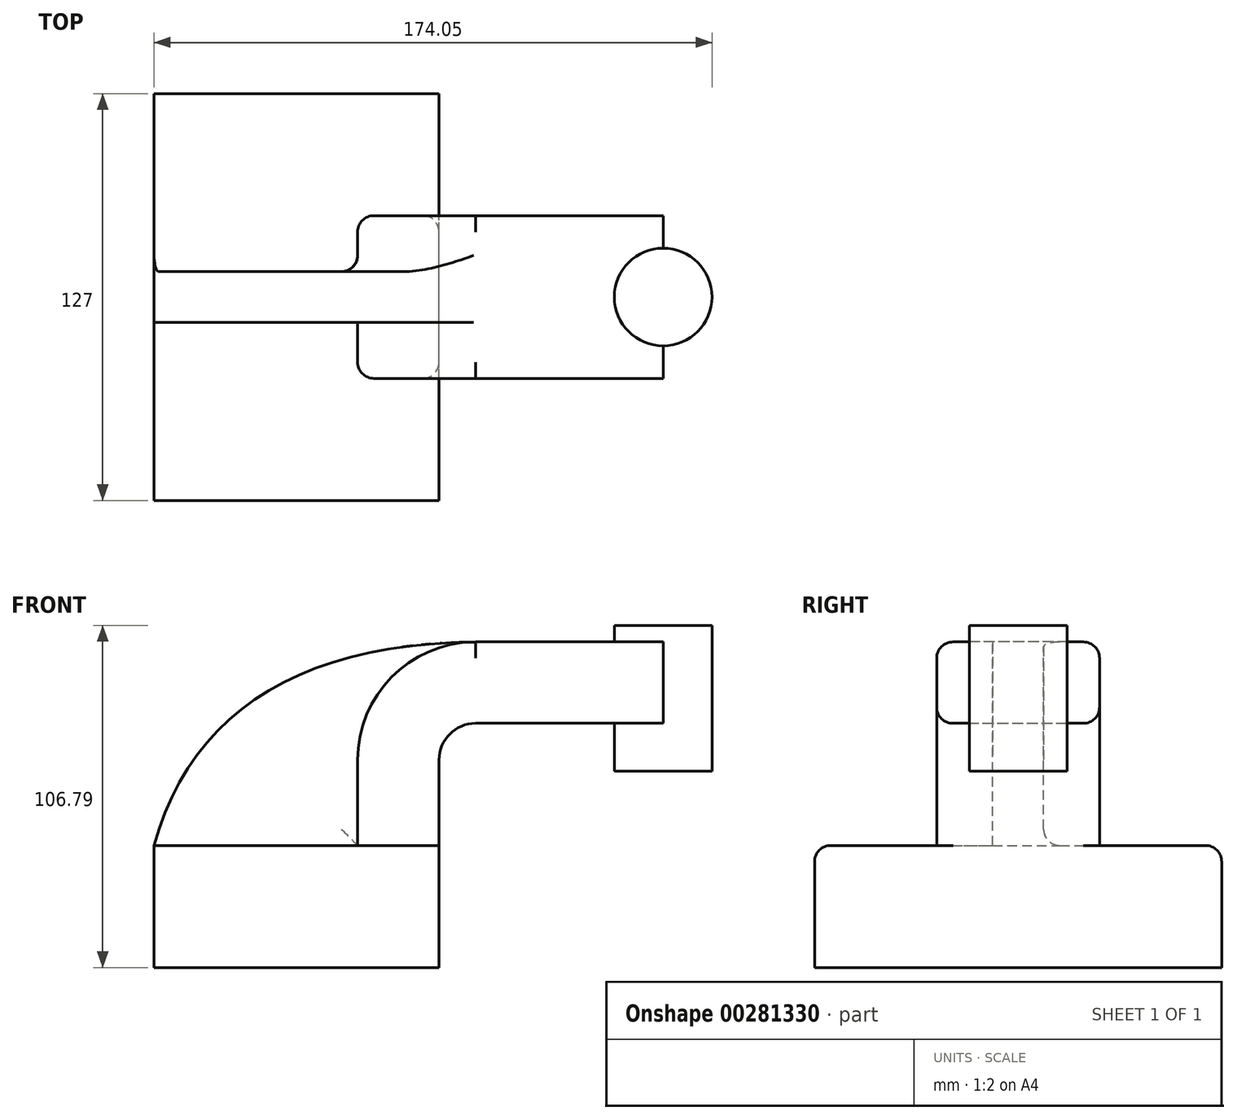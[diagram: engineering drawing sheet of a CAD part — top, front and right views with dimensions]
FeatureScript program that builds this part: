
annotation { "Feature Type Name" : "Feature", "Feature Type Description" : "" }
export const myFeature = defineFeature(function(context is Context, id is Id, definition is map)
    precondition{}
    {
        {
            var Q0;
            Q0=qCreatedBy(makeId("Front.planeOp"),FACE);
            var sketch = newSketch(context, id + "F0", { "sketchPlane" : qUnion([Q0])});
            skLineSegment(sketch, "E0.bottom", {"start": v(44.45, -19.05) * mm, "end": v(-44.45, -19.05) * mm});
            skLineSegment(sketch, "E0.top", {"start": v(44.45, 19.05) * mm, "end": v(-44.45, 19.05) * mm});
            skLineSegment(sketch, "E0.left", {"start": v(44.45, -19.05) * mm, "end": v(44.45, 19.05) * mm});
            skLineSegment(sketch, "E0.right", {"start": v(-44.45, -19.05) * mm, "end": v(-44.45, 19.05) * mm});
            skPoint(sketch, "E0.middle", {"position": v(0, 0) * mm});
            skLineSegment(sketch, "E1.bottom", {"start": v(129.6, 42.19) * mm, "end": v(99.12, 42.19) * mm});
            skLineSegment(sketch, "E1.top", {"start": v(129.6, 87.74) * mm, "end": v(99.12, 87.74) * mm});
            skLineSegment(sketch, "E1.left", {"start": v(129.6, 42.19) * mm, "end": v(129.6, 87.74) * mm});
            skLineSegment(sketch, "E1.right", {"start": v(99.12, 42.19) * mm, "end": v(99.12, 87.74) * mm});
            skPoint(sketch, "E1.middle", {"position": v(114.36, 64.96) * mm});
            skLineSegment(sketch, "E2", {"start": v(44.45, 19.05) * mm, "end": v(44.45, 45.77) * mm});
            skArc(sketch, "E3", {"start": v(44.45, 45.77) * mm, "mid": v(47.79, 53.83) * mm, "end": v(55.85, 57.16) * mm});
            skArc(sketch, "E4.1", {"start": v(19.05, 45.77) * mm, "mid": v(29.83, 71.79) * mm, "end": v(55.85, 82.56) * mm});
            skLineSegment(sketch, "E4.2", {"start": v(19.05, 19.05) * mm, "end": v(19.05, 45.77) * mm});
            skLineSegment(sketch, "E5", {"start": v(55.85, 82.56) * mm, "end": v(114.36, 82.56) * mm});
            skLineSegment(sketch, "E6", {"start": v(114.36, 57.16) * mm, "end": v(55.85, 57.16) * mm});
            skFitSpline(sketch, "E7", {"points": [v(-44.45, 19.05) * mm, v(55.85, 82.56) * mm], "startDerivative": vector(33.5, 123.73) * mm, "endDerivative": vector(164.87, 1.22) * mm});
            skLineSegment(sketch, "E8", {"start": v(114.36, 87.74) * mm, "end": v(114.36, 42.19) * mm});
            skSolve(sketch);
        }
        {
            var Q0;
            Q0=makeQuery(id+"F0.imprint","IMPRINT",FACE,{"disambiguationData":[TD([[makeQuery(id+"F0.imprint","IMPRINT",EDGE,{"derivedFrom":sQuery(id+"F0.wireOp",EDGE,"E0.bottom")}),-1.0]])]});
            extrude(context, id + "F1", {"entities" : qUnion([Q0]), "endBound" : BoundingType.SYMMETRIC, "depth" : 127 * mm});
        }
        {
            var Q0;
            {var subQ1=sQuery(id+"F0.wireOp",EDGE,"E2");Q0=makeQuery(id+"F0.imprint","IMPRINT",FACE,{"disambiguationData":[TD([[makeQuery(id+"F0.imprint","IMPRINT",EDGE,{"derivedFrom":subQ1}),1.0]])]});}
            var Q1;
            {var subQ0=sQuery(id+"F0.wireOp",EDGE,"E6");var subQ1=sQuery(id+"F0.wireOp",EDGE,"E1.right");var subQ2=makeQuery(id+"F0.imprint","INTERSECT",VERTEX,{"derivedFrom":[subQ1,subQ0]});Q1=makeQuery(id+"F0.imprint","IMPRINT",FACE,{"disambiguationData":[TD([[makeQuery(id+"F0.imprint","IMPRINT",EDGE,{"disambiguationData":[TD([[subQ2,-1.0]])],"derivedFrom":subQ1}),-1.0]])]});}
            extrude(context, id + "F2", {"entities" : qUnion([Q0, Q1]), "operationType" : NewBodyOperationType.ADD, "endBound" : BoundingType.SYMMETRIC, "depth" : 50.8 * mm});
        }
        {
            var Q0;
            {var subQ3=sQuery(id+"F0.wireOp",EDGE,"E4.2");Q0=makeQuery(id+"F0.imprint","IMPRINT",FACE,{"disambiguationData":[TD([[makeQuery(id+"F0.imprint","IMPRINT",EDGE,{"derivedFrom":subQ3}),1.0]])]});}
            extrude(context, id + "F3", {"entities" : qUnion([Q0]), "operationType" : NewBodyOperationType.ADD, "endBound" : BoundingType.SYMMETRIC, "depth" : 15.88 * mm});
        }
        {
            var Q0;
            {var subQ4=sQuery(id+"F0.wireOp",EDGE,"E1.left");Q0=makeQuery(id+"F0.imprint","IMPRINT",FACE,{"disambiguationData":[TD([[makeQuery(id+"F0.imprint","IMPRINT",EDGE,{"derivedFrom":subQ4}),1.0]])]});}
            var Q1;
            Q1=sQuery(id+"F0.wireOp",EDGE,"E8");
            revolve(context, id + "F4", {"operationType" : NewBodyOperationType.ADD, "entities" : qUnion([Q0]), "axis" : qUnion([Q1]), "revolveType" : RevolveType.FULL});
        }
        {
            var Q0;
            Q0=makeQuery(id+"F3.opExtrude","CAP_EDGE",EDGE,{"disambiguationData":[OSD([sQuery(id+"F0.wireOp",EDGE,"E0.top")])],"isStart":false});
            var Q1;
            {var subQ0=sQuery(id+"F0.wireOp",EDGE,"E0.top");var subQ1=sQuery(id+"F0.wireOp",EDGE,"E7");var subQ2=sQuery(id+"F0.wireOp",EDGE,"E4.2");var subQ3=sQuery(id+"F0.wireOp",EDGE,"E4.1");Q1=makeQuery(id+"F3.boolean.opBoolean","SPLIT",EDGE,{"disambiguationData":[TD([makeQuery(id+"F3.opExtrude","CAP_FACE",FACE,{"disambiguationData":[OSD([subQ0,subQ3,subQ2,subQ1])],"isStart":false})])],"derivedFrom":makeQuery(id+"F2.opExtrude","SWEPT_EDGE",EDGE,{"disambiguationData":[OSD([subQ0,subQ2])]})});}
            var Q2;
            Q2=makeQuery(id+"F3.opExtrude","CAP_EDGE",EDGE,{"disambiguationData":[OSD([sQuery(id+"F0.wireOp",EDGE,"E4.2")])],"isStart":false});
            var Q3;
            Q3=makeQuery(id+"F3.opExtrude","CAP_EDGE",EDGE,{"disambiguationData":[OSD([sQuery(id+"F0.wireOp",EDGE,"E4.1")])],"isStart":false});
            var Q4;
            Q4=makeQuery(id+"F3.opExtrude","CAP_EDGE",EDGE,{"disambiguationData":[OSD([sQuery(id+"F0.wireOp",EDGE,"E4.1")])],"isStart":true});
            var Q5;
            Q5=makeQuery(id+"F3.opExtrude","CAP_EDGE",EDGE,{"disambiguationData":[OSD([sQuery(id+"F0.wireOp",EDGE,"E0.top")])],"isStart":true});
            var Q6;
            {var subQ0=sQuery(id+"F0.wireOp",EDGE,"E0.top");var subQ1=sQuery(id+"F0.wireOp",EDGE,"E7");var subQ2=sQuery(id+"F0.wireOp",EDGE,"E4.2");var subQ3=sQuery(id+"F0.wireOp",EDGE,"E4.1");Q6=makeQuery(id+"F3.boolean.opBoolean","SPLIT",EDGE,{"disambiguationData":[TD([makeQuery(id+"F3.opExtrude","CAP_FACE",FACE,{"disambiguationData":[OSD([subQ0,subQ3,subQ2,subQ1])],"isStart":true})])],"derivedFrom":makeQuery(id+"F2.opExtrude","SWEPT_EDGE",EDGE,{"disambiguationData":[OSD([subQ0,subQ2])]})});}
            var Q7;
            Q7=makeQuery(id+"F2.opExtrude","CAP_EDGE",EDGE,{"disambiguationData":[OSD([sQuery(id+"F0.wireOp",EDGE,"E0.top")])],"isStart":true});
            var Q8;
            Q8=makeQuery(id+"F2.opExtrude","CAP_EDGE",EDGE,{"disambiguationData":[OSD([sQuery(id+"F0.wireOp",EDGE,"E0.top")])],"isStart":false});
            var Q9;
            Q9=makeQuery(id+"F1.opExtrude","CAP_EDGE",EDGE,{"disambiguationData":[OSD([sQuery(id+"F0.wireOp",EDGE,"E0.top")])],"isStart":false});
            var Q10;
            Q10=makeQuery(id+"F1.opExtrude","CAP_EDGE",EDGE,{"disambiguationData":[OSD([sQuery(id+"F0.wireOp",EDGE,"E0.top")])],"isStart":true});
            var Q11;
            Q11=makeQuery(id+"F2.opExtrude","CAP_EDGE",EDGE,{"disambiguationData":[OSD([sQuery(id+"F0.wireOp",EDGE,"E5")])],"isStart":true});
            var Q12;
            Q12=makeQuery(id+"F2.opExtrude","CAP_EDGE",EDGE,{"disambiguationData":[OSD([sQuery(id+"F0.wireOp",EDGE,"E4.1")])],"isStart":true});
            var Q13;
            Q13=makeQuery(id+"F2.opExtrude","CAP_EDGE",EDGE,{"disambiguationData":[OSD([sQuery(id+"F0.wireOp",EDGE,"E5")])],"isStart":false});
            var Q14;
            Q14=makeQuery(id+"F2.opExtrude","CAP_EDGE",EDGE,{"disambiguationData":[OSD([sQuery(id+"F0.wireOp",EDGE,"E4.1")])],"isStart":false});
            var Q15;
            Q15=makeQuery(id+"F2.opExtrude","CAP_EDGE",EDGE,{"disambiguationData":[OSD([sQuery(id+"F0.wireOp",EDGE,"E2")])],"isStart":false});
            var Q16;
            Q16=makeQuery(id+"F2.opExtrude","CAP_EDGE",EDGE,{"disambiguationData":[OSD([sQuery(id+"F0.wireOp",EDGE,"E6")])],"isStart":true});
            fillet(context, id + "F5", {"entities" : qUnion([Q0, Q1, Q2, Q3, Q4, Q5, Q6, Q7, Q8, Q9, Q10, Q11, Q12, Q13, Q14, Q15, Q16]), "radius" : 5.08 * mm, "tangentPropagation" : true, "allowEdgeOverflow" : false});
        }
    });
